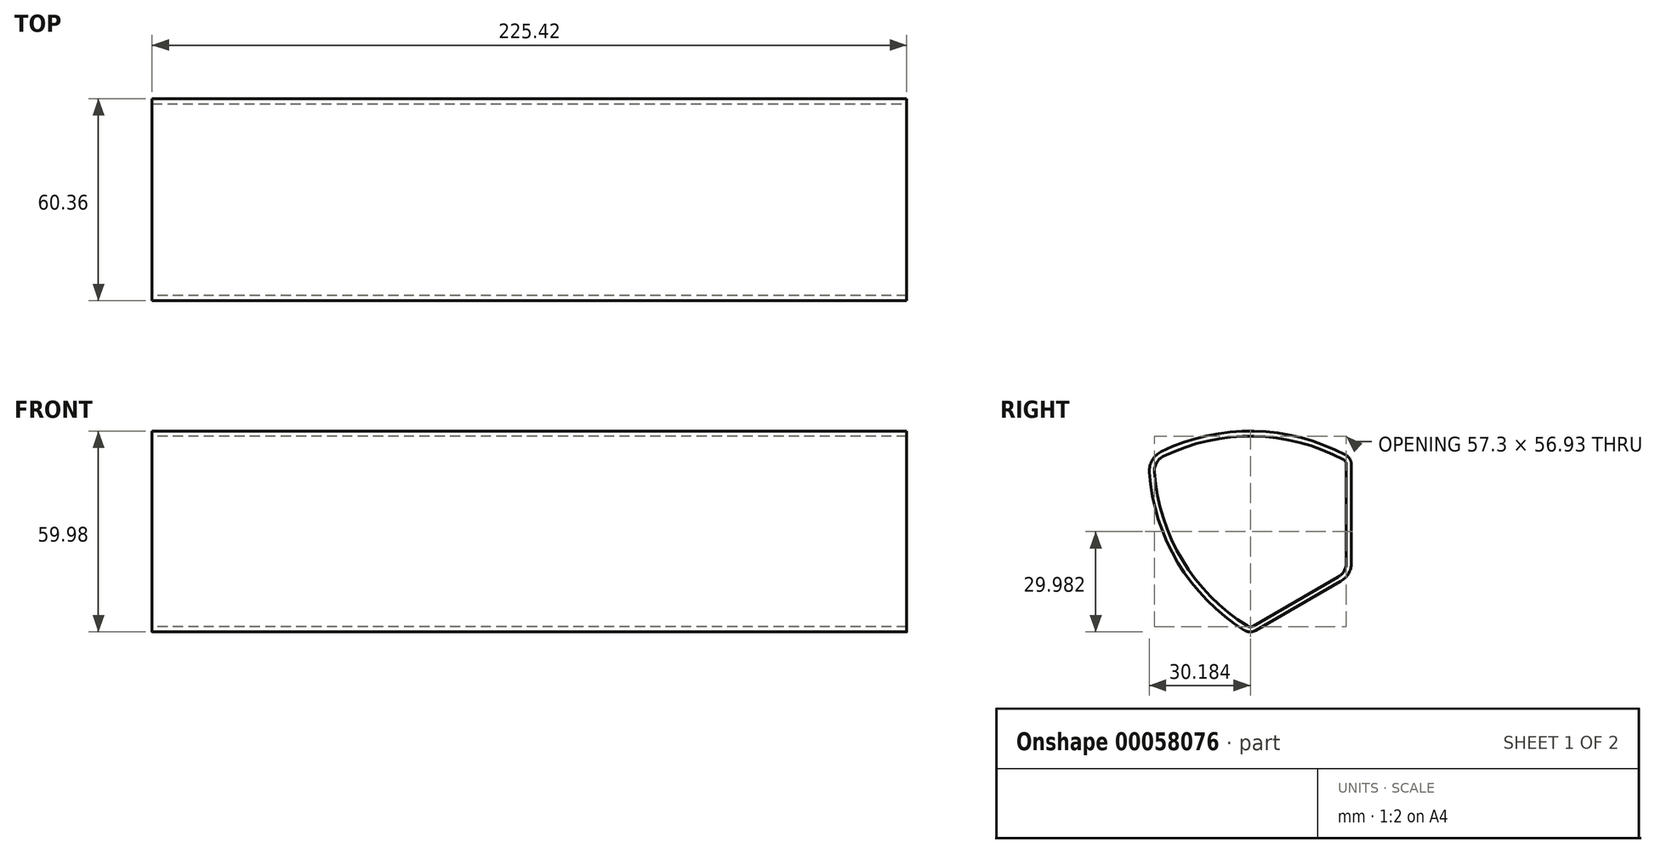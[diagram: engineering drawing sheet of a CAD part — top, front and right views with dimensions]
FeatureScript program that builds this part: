
annotation { "Feature Type Name" : "Feature", "Feature Type Description" : "" }
export const myFeature = defineFeature(function(context is Context, id is Id, definition is map)
    precondition{}
    {
        {
            var Q0;
            Q0=qCreatedBy(makeId("Right.planeOp"),FACE);
            var sketch = newSketch(context, id + "F0", { "sketchPlane" : qUnion([Q0])});
            skLineSegment(sketch, "E0", {"start": v(-30.25, -17.46) * mm, "end": v(0, 0) * mm});
            skLineSegment(sketch, "E1", {"start": v(0, 0) * mm, "end": v(0, 34.93) * mm});
            skArc(sketch, "E2", {"start": v(0, 34.92) * mm, "mid": v(-30.25, 43.03) * mm, "end": v(-60.5, 34.92) * mm});
            skLineSegment(sketch, "E3", {"start": v(0, 34.93) * mm, "end": v(-30.25, -17.46) * mm, "construction": true});
            skPoint(sketch, "E4", {"position": v(-15.12, 8.73) * mm});
            skLineSegment(sketch, "E5", {"start": v(0, 0) * mm, "end": v(-60.5, 34.93) * mm, "construction": true});
            skArc(sketch, "E6", {"start": v(-60.5, 34.92) * mm, "mid": v(-52.39, 4.68) * mm, "end": v(-30.25, -17.46) * mm});
            skLineSegment(sketch, "E7", {"start": v(0, 34.93) * mm, "end": v(-60.5, 34.92) * mm, "construction": true});
            skSolve(sketch);
        }
        {
            var Q0;
            Q0=qSketchRegion(id+"F0",true);
            extrude(context, id + "F1", {"entities" : qUnion([Q0]), "endBound" : BoundingType.SYMMETRIC, "depth" : 225.42 * mm});
        }
        {
            var Q0;
            Q0=makeQuery(id+"F1.opExtrude","SWEPT_EDGE",EDGE,{"disambiguationData":[OSD([sQuery(id+"F0.wireOp",EDGE,"E2"),sQuery(id+"F0.wireOp",EDGE,"E6")])]});
            var Q1;
            Q1=makeQuery(id+"F1.opExtrude","SWEPT_EDGE",EDGE,{"disambiguationData":[OSD([sQuery(id+"F0.wireOp",EDGE,"E0"),sQuery(id+"F0.wireOp",EDGE,"E1")])]});
            fillet(context, id + "F2", {"entities" : qUnion([Q0, Q1]), "radius" : 6.35 * mm, "tangentPropagation" : true, "allowEdgeOverflow" : false});
        }
        {
            var Q0;
            Q0=makeQuery(id+"F1.opExtrude","SWEPT_EDGE",EDGE,{"disambiguationData":[OSD([sQuery(id+"F0.wireOp",EDGE,"E1"),sQuery(id+"F0.wireOp",EDGE,"E2")])]});
            var Q1;
            Q1=makeQuery(id+"F1.opExtrude","SWEPT_EDGE",EDGE,{"disambiguationData":[OSD([sQuery(id+"F0.wireOp",EDGE,"E0"),sQuery(id+"F0.wireOp",EDGE,"E6")])]});
            fillet(context, id + "F3", {"entities" : qUnion([Q0, Q1]), "radius" : 3.17 * mm, "tangentPropagation" : true, "allowEdgeOverflow" : false});
        }
        {
            var Q0;
            Q0=makeQuery(id+"F1.opExtrude","CAP_FACE",FACE,{"disambiguationData":[OSD([sQuery(id+"F0.wireOp",EDGE,"E0"),sQuery(id+"F0.wireOp",EDGE,"E1"),sQuery(id+"F0.wireOp",EDGE,"E2"),sQuery(id+"F0.wireOp",EDGE,"E6")])],"isStart":true});
            var Q1;
            Q1=makeQuery(id+"F1.opExtrude","CAP_FACE",FACE,{"disambiguationData":[OSD([sQuery(id+"F0.wireOp",EDGE,"E0"),sQuery(id+"F0.wireOp",EDGE,"E1"),sQuery(id+"F0.wireOp",EDGE,"E2"),sQuery(id+"F0.wireOp",EDGE,"E6")])],"isStart":false});
            shell(context, id + "F4", {"entities" : qUnion([Q0, Q1]), "thickness" : 1.52 * mm});
        }
    });
